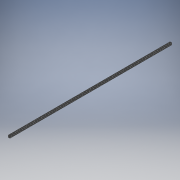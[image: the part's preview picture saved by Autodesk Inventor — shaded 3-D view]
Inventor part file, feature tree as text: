
AUTODESK INVENTOR PART (.ipt)
format: ipt  version: 2018 (Build 220112000, 112)  size: 491,520 bytes
history: native  units: in
note: dims shown in document units (in); Inventor stores cm internally (conversion verified against a paired STEP export)
features: projected_geometry x3, direct_edit x1, extrude x1, sketch x1, other x1, move_body x1
ambient origin geometry x8: Origin, YZ Plane, XZ Plane, XY Plane, X Axis, Y Axis, Z Axis, Center Point
bodies: Solid1 (feature_tree)
feature tree (8):
  direct_edit  "Direct Edit1"
  extrude  "Extrusion1"  Depth=0.813in
  sketch  "Sketch1"  dims[d0=0.0in d1=0.0in d2=122.0472in d3=0.813in d4=0.855in d5=0.855in d6=0.813in d7=0.66in d8=0.0in]
  projected_geometry  "Projected Loop1"
  projected_geometry  "Projected Loop2"
  projected_geometry  "Projected Loop3"
  other  "8020-1515-LS-1515-LS X 145_1_1:1"
  move_body  "Move1"
